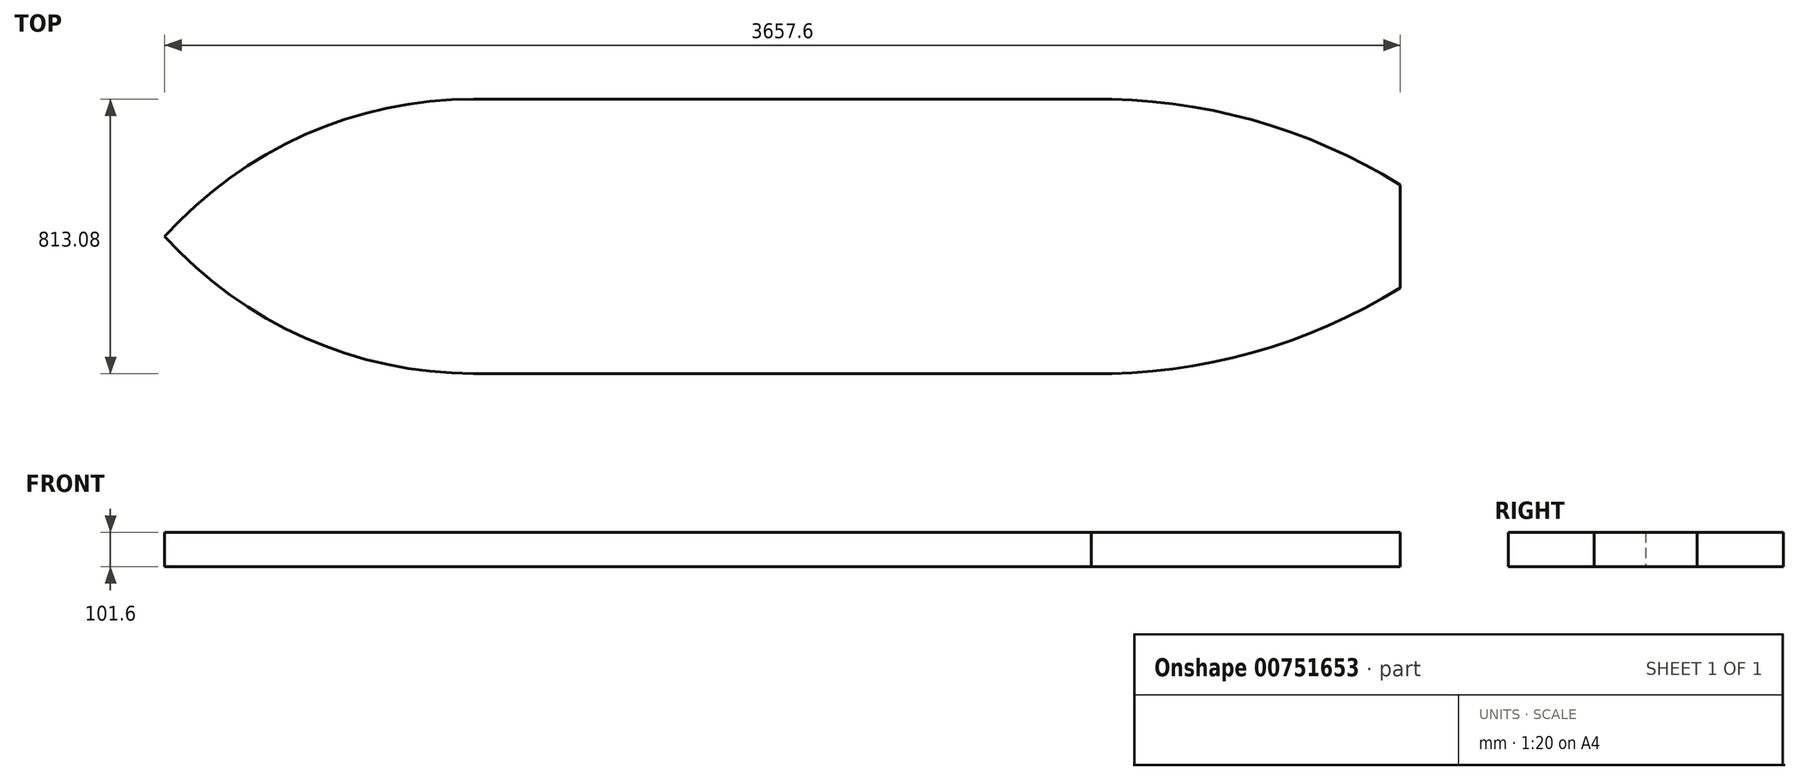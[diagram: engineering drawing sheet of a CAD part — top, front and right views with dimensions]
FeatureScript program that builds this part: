
annotation { "Feature Type Name" : "Feature", "Feature Type Description" : "" }
export const myFeature = defineFeature(function(context is Context, id is Id, definition is map)
    precondition{}
    {
        {
            var Q0;
            Q0=qCreatedBy(makeId("Top.planeOp"),FACE);
            var sketch = newSketch(context, id + "F0", { "sketchPlane" : qUnion([Q0])});
            skPoint(sketch, "E0", {"position": v(-914.4, 406.4) * mm});
            skPoint(sketch, "E1", {"position": v(-914.4, -406.4) * mm});
            skPoint(sketch, "E2", {"position": v(914.4, 406.4) * mm});
            skPoint(sketch, "E3", {"position": v(914.4, -406.4) * mm});
            skPoint(sketch, "E4", {"position": v(1828.8, 0) * mm});
            skPoint(sketch, "E5", {"position": v(1828.8, 152.4) * mm});
            skPoint(sketch, "E6", {"position": v(1828.8, -152.4) * mm});
            skArc(sketch, "E7", {"start": v(1828.8, 152.4) * mm, "mid": v(1389.74, 344.71) * mm, "end": v(914.4, 406.4) * mm});
            skArc(sketch, "E8", {"start": v(914.4, -406.4) * mm, "mid": v(1389.74, -344.71) * mm, "end": v(1828.8, -152.4) * mm});
            skLineSegment(sketch, "E9", {"start": v(1828.8, 152.4) * mm, "end": v(1828.8, -152.4) * mm});
            skPoint(sketch, "E10", {"position": v(0, -406.4) * mm});
            skLineSegment(sketch, "E11", {"start": v(-914.4, -406.4) * mm, "end": v(0, -406.4) * mm});
            skLineSegment(sketch, "E12", {"start": v(0, -406.4) * mm, "end": v(914.4, -406.4) * mm});
            skPoint(sketch, "E13", {"position": v(0, 406.4) * mm});
            skLineSegment(sketch, "E14", {"start": v(-914.4, 406.4) * mm, "end": v(0, 406.4) * mm});
            skLineSegment(sketch, "E15", {"start": v(0, 406.4) * mm, "end": v(914.4, 406.4) * mm});
            skPoint(sketch, "E16", {"position": v(-1828.8, 0) * mm});
            skArc(sketch, "E17", {"start": v(-914.4, 406.4) * mm, "mid": v(-1414.72, 300.22) * mm, "end": v(-1828.8, 0) * mm});
            skArc(sketch, "E18", {"start": v(-1828.8, 0) * mm, "mid": v(-1414.72, -300.22) * mm, "end": v(-914.4, -406.4) * mm});
            skLineSegment(sketch, "E19", {"start": v(-1828.8, 0) * mm, "end": v(-1828.8, -406.4) * mm});
            skLineSegment(sketch, "E20", {"start": v(-914.4, -406.4) * mm, "end": v(-1828.8, -406.4) * mm});
            skLineSegment(sketch, "E21", {"start": v(-914.4, 406.4) * mm, "end": v(-1828.8, 406.4) * mm});
            skLineSegment(sketch, "E22", {"start": v(-1828.8, 406.4) * mm, "end": v(-1828.8, 0) * mm});
            skPoint(sketch, "E23", {"position": v(-1828.8, -406.4) * mm});
            skPoint(sketch, "E24", {"position": v(-1828.8, 406.4) * mm});
            skSolve(sketch);
        }
        {
            var Q0;
            Q0=makeQuery(id+"F0.imprint","IMPRINT",FACE,{"disambiguationData":[TD([[makeQuery(id+"F0.imprint","IMPRINT",EDGE,{"derivedFrom":sQuery(id+"F0.wireOp",EDGE,"E7")}),1.0]])]});
            extrude(context, id + "F1", {"entities" : qUnion([Q0]), "depth" : 50.8 * mm, "offsetDistance" : 25.4 * mm, "hasSecondDirection" : true, "secondDirectionOppositeDirection" : true, "secondDirectionDepth" : 50.8 * mm});
        }
        {
            var Q0;
            Q0=makeQuery(id+"F1.opExtrude","CAP_FACE",FACE,{"disambiguationData":[OSD([sQuery(id+"F0.wireOp",EDGE,"E7"),sQuery(id+"F0.wireOp",EDGE,"E8"),sQuery(id+"F0.wireOp",EDGE,"E9"),sQuery(id+"F0.wireOp",EDGE,"E11"),sQuery(id+"F0.wireOp",EDGE,"E12"),sQuery(id+"F0.wireOp",EDGE,"E14"),sQuery(id+"F0.wireOp",EDGE,"E15"),sQuery(id+"F0.wireOp",EDGE,"E17"),sQuery(id+"F0.wireOp",EDGE,"E18")])],"isStart":false});
            var sketch = newSketch(context, id + "F2", { "sketchPlane" : qUnion([Q0])});
            skPoint(sketch, "E25", {"position": v(-1828.8, 0) * mm});
            skPoint(sketch, "E26", {"position": v(1828.8, 152.4) * mm});
            skPoint(sketch, "E27", {"position": v(1828.8, -152.4) * mm});
            skPoint(sketch, "E28", {"position": v(914.4, 406.4) * mm});
            skPoint(sketch, "E29", {"position": v(914.4, -406.4) * mm});
            skPoint(sketch, "E30", {"position": v(-914.4, -406.4) * mm});
            skPoint(sketch, "E31", {"position": v(-914.4, 406.4) * mm});
            skPoint(sketch, "E32", {"position": v(-609.6, 406.4) * mm});
            skPoint(sketch, "E33", {"position": v(-304.8, 406.4) * mm});
            skPoint(sketch, "E34", {"position": v(0, 406.4) * mm});
            skPoint(sketch, "E35", {"position": v(304.8, 406.4) * mm});
            skPoint(sketch, "E36", {"position": v(609.6, 406.4) * mm});
            skPoint(sketch, "E37", {"position": v(304.8, -406.4) * mm});
            skPoint(sketch, "E38", {"position": v(609.6, -406.4) * mm});
            skPoint(sketch, "E39", {"position": v(0, -406.4) * mm});
            skPoint(sketch, "E40", {"position": v(-304.8, -406.4) * mm});
            skPoint(sketch, "E41", {"position": v(-609.6, -406.4) * mm});
            skSolve(sketch);
        }
        {
            var Q0;
            Q0=makeQuery(id+"F1.opExtrude","SWEPT_FACE",FACE,{"disambiguationData":[OSD([sQuery(id+"F0.wireOp",EDGE,"E11"),sQuery(id+"F0.wireOp",EDGE,"E12")])]});
            var sketch = newSketch(context, id + "F3", { "sketchPlane" : qUnion([Q0])});
            skPoint(sketch, "E42", {"position": v(0, -50.8) * mm});
            skPoint(sketch, "E43", {"position": v(-304.8, -50.8) * mm});
            skPoint(sketch, "E44", {"position": v(-1828.8, -50.8) * mm});
            skPoint(sketch, "E45", {"position": v(-1828.8, 12.7) * mm});
            skArc(sketch, "E46", {"start": v(-1828.8, 12.7) * mm, "mid": v(-1067.64, -39.18) * mm, "end": v(-304.8, -50.8) * mm});
            skPoint(sketch, "E47", {"position": v(914.4, -50.8) * mm});
            skPoint(sketch, "E48", {"position": v(1828.8, -50.8) * mm});
            skPoint(sketch, "E49", {"position": v(1828.8, 12.7) * mm});
            skArc(sketch, "E50", {"start": v(914.4, -50.8) * mm, "mid": v(1372.7, -34.9) * mm, "end": v(1828.8, 12.7) * mm});
            skLineSegment(sketch, "E51", {"start": v(-304.8, -50.8) * mm, "end": v(914.4, -50.8) * mm});
            skSolve(sketch);
        }
        {
            var Q0;
            Q0 = qConstructionFilter(qBodyType(qCreatedBy(id + "F3" ,EDGE), BodyType.WIRE), ConstructionObject.NO);
            extrude(context, id + "F4", {"bodyType" : ToolBodyType.SURFACE, "surfaceEntities" : qUnion([Q0]), "oppositeDirection" : true, "depth" : 812.8 * mm, "offsetDistance" : 25.4 * mm});
        }
    });
